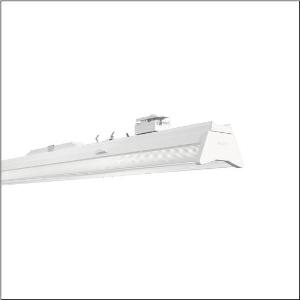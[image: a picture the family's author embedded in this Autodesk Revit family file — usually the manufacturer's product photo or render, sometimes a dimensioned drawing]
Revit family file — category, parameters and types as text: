
# Revit family: licross_r__21_performance_mo_51td16vnd45g_fcc4
name_source: partatom
category: Lighting Fixtures
units: mm (PartAtom-declared; Revit-internal decimal feet)

## family parameters
Cut with Voids When Loaded = No
Host = Face
Light Source = No
Part Type = Normal
Room Calculation Point = No
Round Connector Dimension = Use Diameter
Shared = No

## types (1)
- --- (1 x LED, 4500 lm, 26.3 W, 4000K)
    Apparent Load = 26 VA
    CIE Flux Codes = 66 88 96 79 100
    Color Rendering = 90
    Color Temperature = 4000K
    Default Elevation = 1800 mm
    Description = Licross® 21 Performance MO, luminaire insert, of sheet steel, galvanised, coil coated, white, length: 1.500mm, width: 120mm, height: 123mm, LED rated luminous flux: 4.500lm, light colour: 940, SDCM (Standard Deviation of Colour Matching)MacAdam ≤ 2 SDCM (initial), control gear: DALI 2, CLO, with plug, 5-pole, with phase selection, mains connection: 220..240V, AC, 50/60Hz, start of lifetime: 26W, end of service life: 29W, internal wiring halogen-free, primary light control with lens, of plastic, primary optical cover: cover, of PMMA, light emission: direct/indirect distribution, primary light characteristic: symmetric, protection rating (complete): IP54, insulation class (complete): insulation class I (protective earthing), certification: CE, ENEC, VDE, UKCA, protection symbol: D if used in an environment with non-conductive dust loads with corresponding accessories, impact resistance: IK06, permissible ambient temperature for indoor applications: -25..+45°C, corresponds to IFS (International Featured Standards) requirements for safety and quality in the food industry, reducing of maximum allowable ambient temperature of 5°C with ceiling mounting, LABS conformity tested according to VDMA 24364:2018-05, packaging unit: 1 piece
    Height = 114 mm
    Lamp = 1 x LED
    Lamp Light Flux = 4500 lm
    Lamp Power = 26.3 W
    Lamp count = 1
    Length = 1500 mm
    Luminous efficacy = 171 lm/W
    Manufacturer = Siteco
    ModVariant = No
    Model = 51TD16VND45G
    Mounting Place = Ceiling
    Mounting Type = Pendant
    Number of Poles = 1
    OnlyDefault = Yes
    Power Factor = 1
    Product Name = Licross® 21 Performance MO
    Product group = luminaire insert | ceiling pendant
    ProductGroupID = 901
    Protection Class = Protection class I
    Protection Degree = IP 54
    RLX_Detail_Level = 1
    RLX_Emergency_Light_Flux = 0 lm
    RLX_Emergency_Type = 0
    RLX_Emergency_Type_DB = No
    RlxData = <blob elided: 33837 chars, md5=a7f10d13>
    Socket = socket
    Standby Power = 0 W
    System Light Flux = 4500 lm
    System Power = 26 W
    Type Comments = factory setting: luminous flux: 100 % | dim-lin: 254 | 174 mA
    Type Image = l_1256138.jpg
    URL = http://relux.com
    VarID = @adj_058843
    Voltage = 0 V
    Weight = 0.00 kg
    Width = 120 mm

## geometry (parser evidence)
native form markers: Blend x4, Sweep x13
no freeform markers — native parametric forms only
